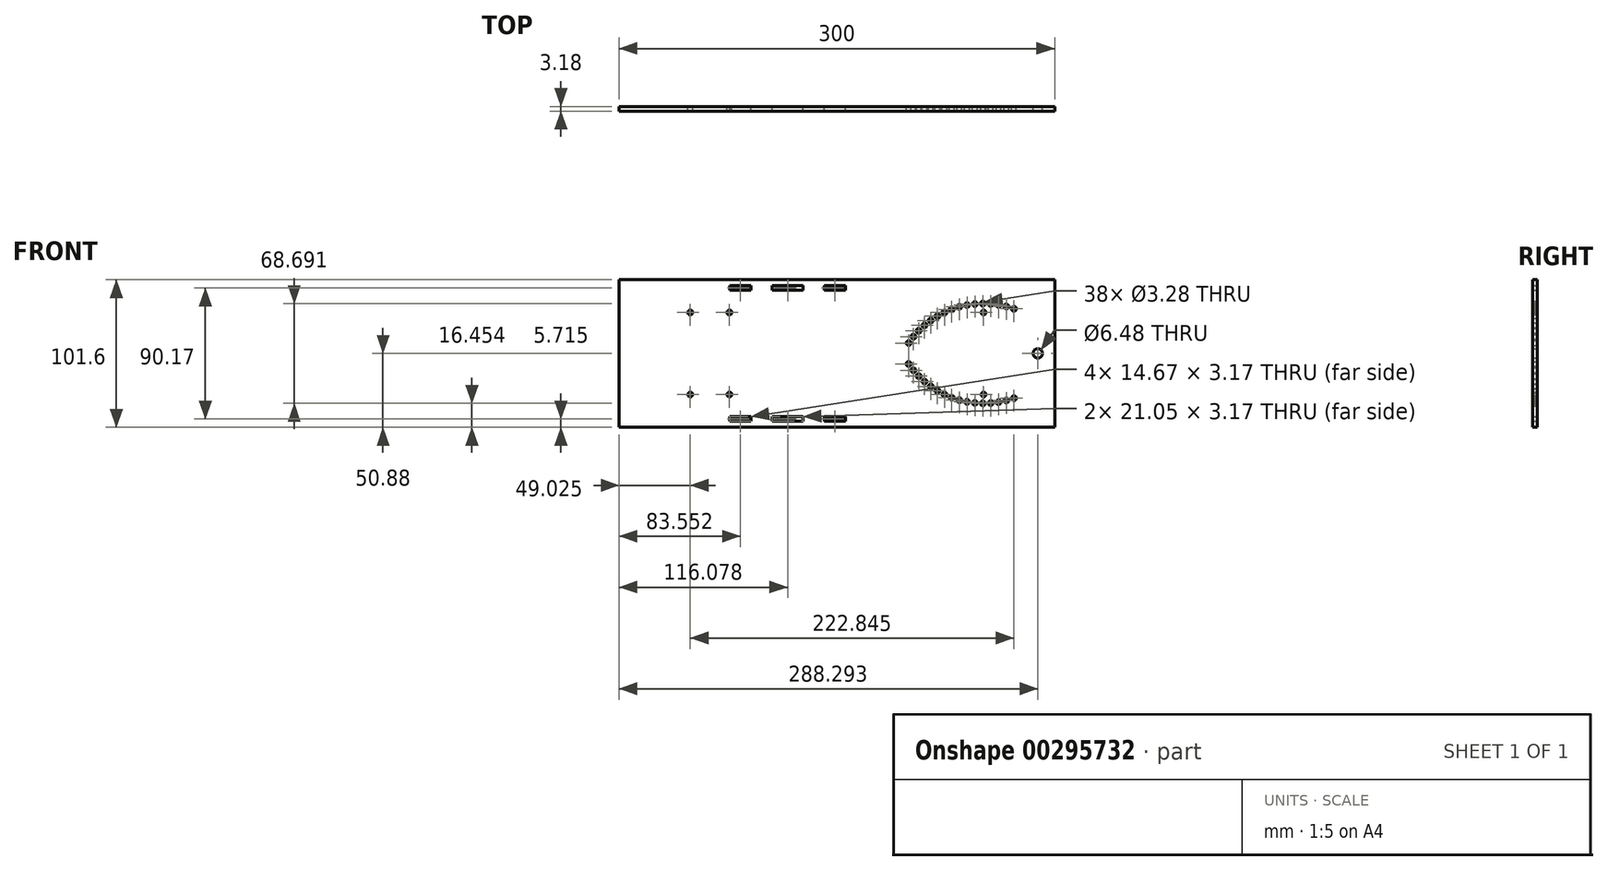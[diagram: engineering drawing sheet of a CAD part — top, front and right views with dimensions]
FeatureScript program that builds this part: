
annotation { "Feature Type Name" : "Feature", "Feature Type Description" : "" }
export const myFeature = defineFeature(function(context is Context, id is Id, definition is map)
    precondition{}
    {
        {
            var Q0;
            Q0=qCreatedBy(makeId("Front.planeOp"),FACE);
            var sketch = newSketch(context, id + "F0", { "sketchPlane" : qUnion([Q0])});
            skLineSegment(sketch, "E0.bottom", {"start": v(150, -50.8) * mm, "end": v(-150, -50.8) * mm});
            skLineSegment(sketch, "E0.top", {"start": v(150, 50.8) * mm, "end": v(-150, 50.8) * mm});
            skLineSegment(sketch, "E0.left", {"start": v(150, -50.8) * mm, "end": v(150, 50.8) * mm});
            skLineSegment(sketch, "E0.right", {"start": v(-150, -50.8) * mm, "end": v(-150, 50.8) * mm});
            skPoint(sketch, "E0.middle", {"position": v(0, 0) * mm});
            skCircle(sketch, "E1", {"center": v(-87.5, 28.25) * mm, "radius": 4 * mm, "construction": true});
            skLineSegment(sketch, "E2", {"start": v(-87.5, 28.25) * mm, "end": v(-83.5, 28.25) * mm, "construction": true});
            skLineSegment(sketch, "E3", {"start": v(-87.5, 28.25) * mm, "end": v(-87.5, 32.25) * mm, "construction": true});
            skCircle(sketch, "E4", {"center": v(-74.03, 28.25) * mm, "radius": 1.64 * mm});
            skCircle(sketch, "E5.MirrorC", {"center": v(-100.97, 28.25) * mm, "radius": 1.64 * mm});
            skCircle(sketch, "E6", {"center": v(-87.5, -28.25) * mm, "radius": 4 * mm, "construction": true});
            skLineSegment(sketch, "E7", {"start": v(-87.5, -28.25) * mm, "end": v(-83.5, -28.25) * mm, "construction": true});
            skLineSegment(sketch, "E8", {"start": v(-87.5, -28.25) * mm, "end": v(-87.5, -24.25) * mm, "construction": true});
            skCircle(sketch, "E9", {"center": v(-74.03, -28.25) * mm, "radius": 1.64 * mm});
            skCircle(sketch, "E10.MirrorC", {"center": v(-100.97, -28.25) * mm, "radius": 1.64 * mm});
            skCircle(sketch, "E11", {"center": v(87.5, -28.25) * mm, "radius": 4 * mm, "construction": true});
            skLineSegment(sketch, "E12", {"start": v(87.5, -28.25) * mm, "end": v(91.5, -28.25) * mm, "construction": true});
            skLineSegment(sketch, "E13", {"start": v(87.5, -28.25) * mm, "end": v(87.5, -24.25) * mm, "construction": true});
            skCircle(sketch, "E14", {"center": v(100.97, -28.25) * mm, "radius": 1.64 * mm});
            skCircle(sketch, "E15.MirrorC", {"center": v(74.03, -28.25) * mm, "radius": 1.64 * mm});
            skCircle(sketch, "E16", {"center": v(87.5, 28.25) * mm, "radius": 4 * mm, "construction": true});
            skLineSegment(sketch, "E17", {"start": v(87.5, 28.25) * mm, "end": v(91.5, 28.25) * mm, "construction": true});
            skLineSegment(sketch, "E18", {"start": v(87.5, 28.25) * mm, "end": v(87.5, 32.25) * mm, "construction": true});
            skCircle(sketch, "E19", {"center": v(100.97, 28.25) * mm, "radius": 1.64 * mm});
            skCircle(sketch, "E20.MirrorC", {"center": v(74.03, 28.25) * mm, "radius": 1.64 * mm});
            skLineSegment(sketch, "E21.bottom", {"start": v(-59.11, -46.67) * mm, "end": v(-73.78, -46.67) * mm});
            skLineSegment(sketch, "E21.top", {"start": v(-59.11, -43.5) * mm, "end": v(-73.78, -43.5) * mm});
            skLineSegment(sketch, "E21.left", {"start": v(-59.11, -46.67) * mm, "end": v(-59.11, -43.5) * mm});
            skLineSegment(sketch, "E21.right", {"start": v(-73.78, -46.67) * mm, "end": v(-73.78, -43.5) * mm});
            skPoint(sketch, "E21.middle", {"position": v(-66.45, -45.09) * mm});
            skLineSegment(sketch, "E22.bottom", {"start": v(-29.78, -46.67) * mm, "end": v(-44.45, -46.67) * mm});
            skLineSegment(sketch, "E22.top", {"start": v(-29.78, -43.5) * mm, "end": v(-44.45, -43.5) * mm});
            skLineSegment(sketch, "E22.left", {"start": v(-29.78, -46.67) * mm, "end": v(-29.78, -43.5) * mm, "construction": true});
            skLineSegment(sketch, "E22.right", {"start": v(-44.45, -46.67) * mm, "end": v(-44.45, -43.5) * mm});
            skPoint(sketch, "E22.middle", {"position": v(-37.11, -45.09) * mm});
            skLineSegment(sketch, "E23.bottom", {"start": v(-55.75, -57.15) * mm, "end": v(-119.25, -57.15) * mm, "construction": true});
            skLineSegment(sketch, "E23.top", {"start": v(-55.75, -50.8) * mm, "end": v(-119.25, -50.8) * mm, "construction": true});
            skLineSegment(sketch, "E23.left", {"start": v(-55.75, -57.15) * mm, "end": v(-55.75, -50.8) * mm, "construction": true});
            skLineSegment(sketch, "E23.right", {"start": v(-119.25, -57.15) * mm, "end": v(-119.25, -50.8) * mm, "construction": true});
            skPoint(sketch, "E23.middle", {"position": v(-87.5, -53.98) * mm});
            skPoint(sketch, "E23.middle.positionSnap0", {"position": v(-87.5, -26.25) * mm});
            skPoint(sketch, "E23.centerSnap0", {"position": v(-87.5, -26.25) * mm});
            skLineSegment(sketch, "E24.bottom", {"start": v(-55.75, -50.8) * mm, "end": v(-47.81, -50.8) * mm, "construction": true});
            skLineSegment(sketch, "E24.top", {"start": v(-55.75, -57.15) * mm, "end": v(-47.81, -57.15) * mm, "construction": true});
            skLineSegment(sketch, "E24.left", {"start": v(-55.75, -50.8) * mm, "end": v(-55.75, -57.15) * mm, "construction": true});
            skLineSegment(sketch, "E24.right", {"start": v(-47.81, -50.8) * mm, "end": v(-47.81, -57.15) * mm, "construction": true});
            skLineSegment(sketch, "E25", {"start": v(-59.11, -43.5) * mm, "end": v(-44.45, -46.67) * mm, "construction": true});
            skPoint(sketch, "E26", {"position": v(-51.78, -45.08) * mm});
            skPoint(sketch, "E27", {"position": v(-51.78, -50.8) * mm});
            skLineSegment(sketch, "E28", {"start": v(-51.78, -50.8) * mm, "end": v(-51.78, -57.15) * mm, "construction": true});
            skLineSegment(sketch, "E29.MirrorCS", {"start": v(-55.75, 50.8) * mm, "end": v(-119.25, 50.8) * mm, "construction": true});
            skLineSegment(sketch, "E30.MirrorCS", {"start": v(-55.75, 50.8) * mm, "end": v(-47.81, 50.8) * mm, "construction": true});
            skLineSegment(sketch, "E31.MirrorCS", {"start": v(-55.75, 57.15) * mm, "end": v(-119.25, 57.15) * mm, "construction": true});
            skLineSegment(sketch, "E32.MirrorCS", {"start": v(-119.25, 57.15) * mm, "end": v(-119.25, 50.8) * mm, "construction": true});
            skLineSegment(sketch, "E33.MirrorCS", {"start": v(-55.75, 57.15) * mm, "end": v(-47.81, 57.15) * mm, "construction": true});
            skLineSegment(sketch, "E34.MirrorCS", {"start": v(-55.75, 50.8) * mm, "end": v(-55.75, 57.15) * mm, "construction": true});
            skLineSegment(sketch, "E35.MirrorCS", {"start": v(-51.78, 50.8) * mm, "end": v(-51.78, 57.15) * mm, "construction": true});
            skLineSegment(sketch, "E36.MirrorCS", {"start": v(-47.81, 50.8) * mm, "end": v(-47.81, 57.15) * mm, "construction": true});
            skLineSegment(sketch, "E37.MirrorCS", {"start": v(-59.11, 46.67) * mm, "end": v(-59.11, 43.5) * mm});
            skLineSegment(sketch, "E38.MirrorCS", {"start": v(-59.11, 43.5) * mm, "end": v(-73.78, 43.5) * mm});
            skLineSegment(sketch, "E39.MirrorCS", {"start": v(-73.78, 46.67) * mm, "end": v(-73.78, 43.5) * mm});
            skLineSegment(sketch, "E40.MirrorCS", {"start": v(-59.11, 46.67) * mm, "end": v(-73.78, 46.67) * mm});
            skCircle(sketch, "E41", {"center": v(138.3, 0.08) * mm, "radius": 3.24 * mm});
            skLineSegment(sketch, "E42.bottom", {"start": v(-38.06, -43.5) * mm, "end": v(-23.4, -43.5) * mm});
            skLineSegment(sketch, "E42.top", {"start": v(-38.06, -46.67) * mm, "end": v(-23.4, -46.67) * mm});
            skLineSegment(sketch, "E42.left", {"start": v(-38.06, -43.5) * mm, "end": v(-38.06, -46.67) * mm, "construction": true});
            skLineSegment(sketch, "E42.right", {"start": v(-23.4, -43.5) * mm, "end": v(-23.4, -46.67) * mm});
            skLineSegment(sketch, "E43.bottom", {"start": v(-8.73, -43.5) * mm, "end": v(5.94, -43.5) * mm});
            skLineSegment(sketch, "E43.top", {"start": v(-8.73, -46.67) * mm, "end": v(5.94, -46.67) * mm});
            skLineSegment(sketch, "E43.left", {"start": v(-8.73, -43.5) * mm, "end": v(-8.73, -46.67) * mm});
            skLineSegment(sketch, "E43.right", {"start": v(5.94, -43.5) * mm, "end": v(5.94, -46.67) * mm});
            skLineSegment(sketch, "E44", {"start": v(-23.4, -43.5) * mm, "end": v(-8.73, -46.67) * mm, "construction": true});
            skPoint(sketch, "E45", {"position": v(-16.06, -45.09) * mm});
            skLineSegment(sketch, "E46", {"start": v(-16.06, -50.8) * mm, "end": v(-16.06, -57.52) * mm, "construction": true});
            skPoint(sketch, "E46.startSnap0", {"position": v(0, -50.8) * mm});
            skLineSegment(sketch, "E47.MirrorCS", {"start": v(5.94, 43.5) * mm, "end": v(5.94, 46.67) * mm});
            skLineSegment(sketch, "E48.MirrorCS", {"start": v(-23.4, 43.5) * mm, "end": v(-23.4, 46.67) * mm});
            skLineSegment(sketch, "E49.MirrorCS", {"start": v(-44.45, 46.67) * mm, "end": v(-44.45, 43.5) * mm});
            skLineSegment(sketch, "E50.MirrorCS", {"start": v(-8.73, 43.5) * mm, "end": v(-8.73, 46.67) * mm});
            skLineSegment(sketch, "E51.MirrorCS", {"start": v(-29.78, 46.67) * mm, "end": v(-29.78, 43.5) * mm, "construction": true});
            skLineSegment(sketch, "E52.MirrorCS", {"start": v(-23.4, 43.5) * mm, "end": v(-8.73, 46.67) * mm, "construction": true});
            skLineSegment(sketch, "E53.MirrorCS", {"start": v(-38.06, 43.5) * mm, "end": v(-38.06, 46.67) * mm, "construction": true});
            skLineSegment(sketch, "E54.MirrorCS", {"start": v(-8.73, 43.5) * mm, "end": v(5.94, 43.5) * mm});
            skPoint(sketch, "E55.MirrorP", {"position": v(-37.11, 45.09) * mm});
            skLineSegment(sketch, "E56.MirrorCS", {"start": v(-38.06, 43.5) * mm, "end": v(-23.4, 43.5) * mm});
            skLineSegment(sketch, "E57.MirrorCS", {"start": v(-29.78, 43.5) * mm, "end": v(-44.45, 43.5) * mm});
            skLineSegment(sketch, "E58.MirrorCS", {"start": v(-8.73, 46.67) * mm, "end": v(5.94, 46.67) * mm});
            skPoint(sketch, "E59.MirrorP", {"position": v(-16.06, 45.09) * mm});
            skLineSegment(sketch, "E60.MirrorCS", {"start": v(-29.78, 46.67) * mm, "end": v(-44.45, 46.67) * mm});
            skLineSegment(sketch, "E61.MirrorCS", {"start": v(-38.06, 46.67) * mm, "end": v(-23.4, 46.67) * mm});
            skPoint(sketch, "E62.MirrorP", {"position": v(0, 50.8) * mm});
            skCircle(sketch, "E63.1.0", {"center": v(69.2, -25.69) * mm, "radius": 1.64 * mm});
            skCircle(sketch, "E63.2.0", {"center": v(64.62, -22.71) * mm, "radius": 1.64 * mm});
            skCircle(sketch, "E63.3.0", {"center": v(60.32, -19.35) * mm, "radius": 1.64 * mm});
            skCircle(sketch, "E63.4.0", {"center": v(56.33, -15.63) * mm, "radius": 1.64 * mm});
            skCircle(sketch, "E63.5.0", {"center": v(52.67, -11.57) * mm, "radius": 1.64 * mm});
            skCircle(sketch, "E63.6.0", {"center": v(49.39, -7.2) * mm, "radius": 1.64 * mm});
            skLineSegment(sketch, "E63.anchor1", {"start": v(100.97, 28.25) * mm, "end": v(74.03, -28.25) * mm, "construction": true});
            skLineSegment(sketch, "E63.anchor2", {"start": v(100.97, 28.25) * mm, "end": v(41.97, 7.35) * mm, "construction": true});
            skCircle(sketch, "E64.MirrorC", {"center": v(121.87, -30.76) * mm, "radius": 1.64 * mm});
            skCircle(sketch, "E65.MirrorC", {"center": v(116.65, -32.35) * mm, "radius": 1.64 * mm});
            skCircle(sketch, "E66.MirrorC", {"center": v(111.3, -33.49) * mm, "radius": 1.64 * mm});
            skCircle(sketch, "E67.MirrorC", {"center": v(105.89, -34.16) * mm, "radius": 1.64 * mm});
            skCircle(sketch, "E68.MirrorC", {"center": v(100.43, -34.35) * mm, "radius": 1.64 * mm});
            skCircle(sketch, "E69.MirrorC", {"center": v(94.97, -34.06) * mm, "radius": 1.64 * mm});
            skCircle(sketch, "E70.MirrorC", {"center": v(89.57, -33.3) * mm, "radius": 1.64 * mm});
            skCircle(sketch, "E71.MirrorC", {"center": v(84.25, -32.07) * mm, "radius": 1.64 * mm});
            skCircle(sketch, "E72.MirrorC", {"center": v(79.05, -30.38) * mm, "radius": 1.64 * mm});
            skCircle(sketch, "E73.1.0", {"center": v(79.05, 30.38) * mm, "radius": 1.64 * mm});
            skCircle(sketch, "E73.2.0", {"center": v(84.25, 32.07) * mm, "radius": 1.64 * mm});
            skCircle(sketch, "E73.3.0", {"center": v(89.57, 33.3) * mm, "radius": 1.64 * mm});
            skCircle(sketch, "E73.4.0", {"center": v(94.97, 34.06) * mm, "radius": 1.64 * mm});
            skCircle(sketch, "E73.5.0", {"center": v(100.43, 34.35) * mm, "radius": 1.64 * mm});
            skCircle(sketch, "E73.6.0", {"center": v(105.89, 34.16) * mm, "radius": 1.64 * mm});
            skCircle(sketch, "E73.7.0", {"center": v(111.3, 33.49) * mm, "radius": 1.64 * mm});
            skCircle(sketch, "E73.8.0", {"center": v(116.65, 32.35) * mm, "radius": 1.64 * mm});
            skCircle(sketch, "E73.9.0", {"center": v(121.87, 30.76) * mm, "radius": 1.64 * mm});
            skLineSegment(sketch, "E73.anchor1", {"start": v(100.97, -28.25) * mm, "end": v(74.03, 28.25) * mm, "construction": true});
            skLineSegment(sketch, "E73.anchor2", {"start": v(100.97, -28.25) * mm, "end": v(121.87, 30.76) * mm, "construction": true});
            skCircle(sketch, "E74.MirrorC", {"center": v(69.2, 25.69) * mm, "radius": 1.64 * mm});
            skCircle(sketch, "E75.MirrorC", {"center": v(64.62, 22.71) * mm, "radius": 1.64 * mm});
            skCircle(sketch, "E76.MirrorC", {"center": v(60.32, 19.35) * mm, "radius": 1.64 * mm});
            skCircle(sketch, "E77.MirrorC", {"center": v(56.33, 15.63) * mm, "radius": 1.64 * mm});
            skCircle(sketch, "E78.MirrorC", {"center": v(52.67, 11.57) * mm, "radius": 1.64 * mm});
            skCircle(sketch, "E79.MirrorC", {"center": v(49.39, 7.2) * mm, "radius": 1.64 * mm});
            skSolve(sketch);
        }
        {
            var Q0;
            Q0=qSketchRegion(id+"F0",true);
            extrude(context, id + "F1", {"entities" : qUnion([Q0]), "depth" : 3.17 * mm});
        }
    });
